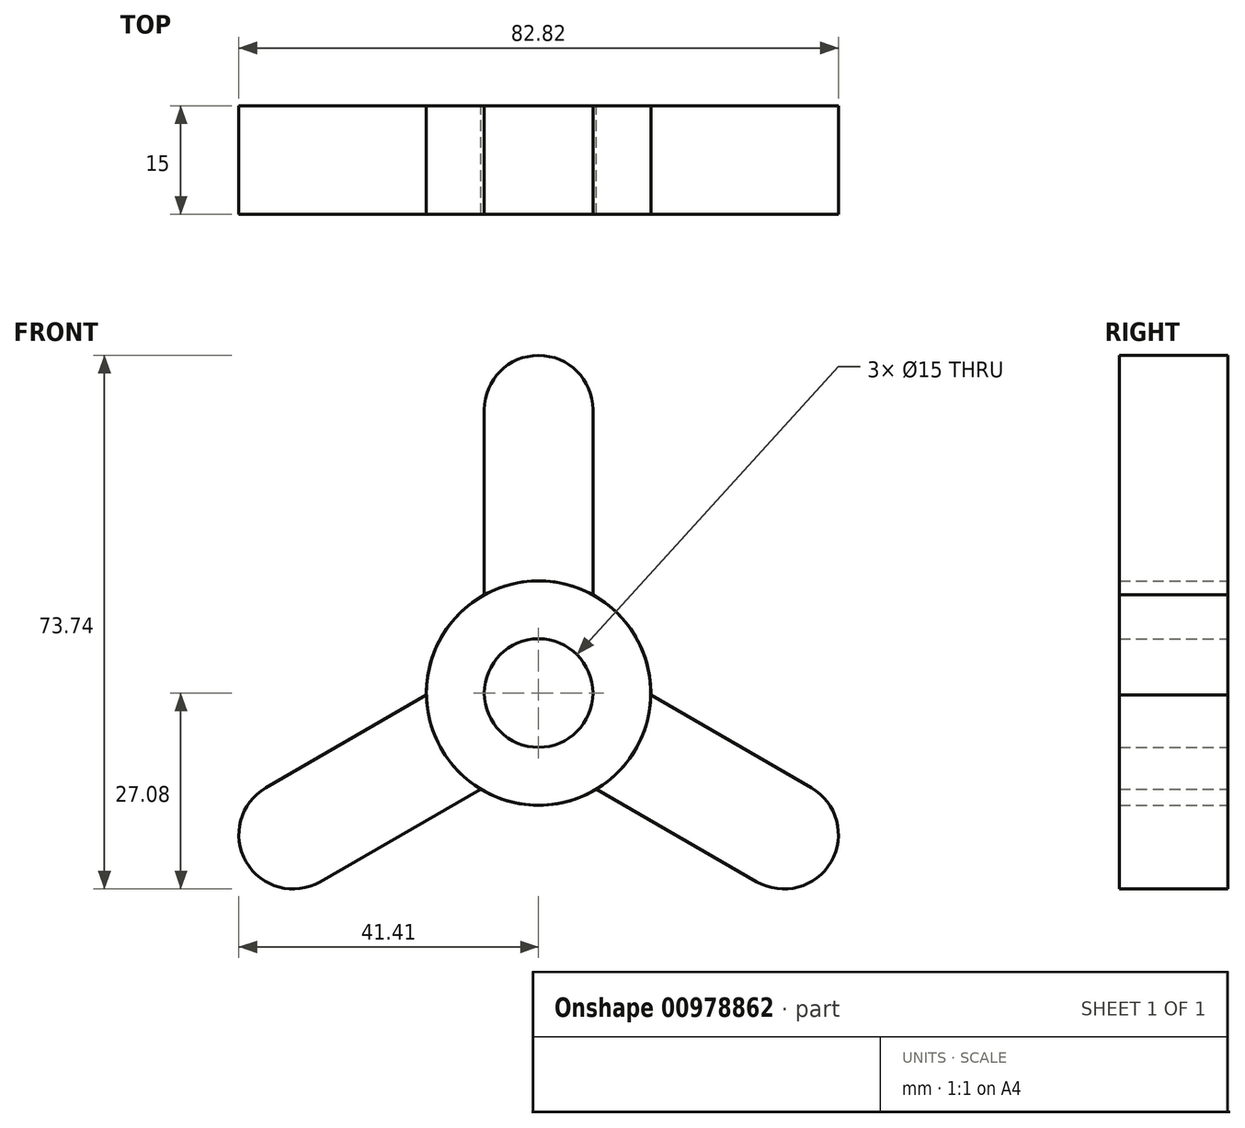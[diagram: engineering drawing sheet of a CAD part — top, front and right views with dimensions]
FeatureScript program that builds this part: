
annotation { "Feature Type Name" : "Feature", "Feature Type Description" : "" }
export const myFeature = defineFeature(function(context is Context, id is Id, definition is map)
    precondition{}
    {
        {
            var Q0;
            Q0=qCreatedBy(makeId("Front.planeOp"),FACE);
            var sketch = newSketch(context, id + "F0", { "sketchPlane" : qUnion([Q0])});
            skCircle(sketch, "E0", {"center": v(0, 0) * mm, "radius": 7.5 * mm});
            skCircle(sketch, "E1.0", {"center": v(0, 0) * mm, "radius": 15.5 * mm});
            skSolve(sketch);
        }
        {
            var Q0;
            Q0 = qSketchRegion(id + "F0", true);
            extrude(context, id + "F1", {"entities" : qUnion([Q0]), "depth" : 15 * mm, "offsetDistance" : 25 * mm});
        }
        {
            var Q0;
            Q0=qCreatedBy(makeId("Front.planeOp"),FACE);
            var sketch = newSketch(context, id + "F2", { "sketchPlane" : qUnion([Q0])});
            skArc(sketch, "E2.0.startCap", {"start": v(-7.5, 39.16) * mm, "mid": v(0, 46.66) * mm, "end": v(7.5, 39.16) * mm});
            skLineSegment(sketch, "E2.0.left", {"start": v(7.5, 39.16) * mm, "end": v(7.5, 13.56) * mm});
            skLineSegment(sketch, "E2.0.right", {"start": v(-7.5, 39.16) * mm, "end": v(-7.5, 13.56) * mm});
            skArc(sketch, "E3.0", {"start": v(7.5, 13.56) * mm, "mid": v(0, 15.5) * mm, "end": v(-7.5, 13.56) * mm});
            skSolve(sketch);
        }
        {
            var Q0;
            Q0 = qSketchRegion(id + "F2", true);
            var Q1;
            Q1=makeQuery(id+"F1.opExtrude","CAP_FACE",FACE,{"disambiguationData":[OSD([sQuery(id+"F0.wireOp",EDGE,"E0"),sQuery(id+"F0.wireOp",EDGE,"E1.0")])],"isStart":false});
            extrude(context, id + "F3", {"entities" : qUnion([Q0]), "operationType" : NewBodyOperationType.ADD, "endBound" : BoundingType.UP_TO_SURFACE, "depth" : 25 * mm, "endBoundEntityFace" : qUnion([Q1]), "offsetDistance" : 25 * mm});
        }
        {
            var Q0;
            Q0=makeQuery(id+"F1.opExtrude","SWEPT_BODY",BODY,{"disambiguationData":[OSD([sQuery(id+"F0.wireOp",EDGE,"E0"),sQuery(id+"F0.wireOp",EDGE,"E1.0")])]});
            var Q1;
            Q1=makeQuery(id+"F1.opExtrude","CAP_EDGE",EDGE,{"disambiguationData":[OSD([sQuery(id+"F0.wireOp",EDGE,"E0")])],"isStart":false});
            circularPattern(context, id + "F4", {"entities" : qUnion([Q0]), "axis" : qUnion([Q1]), "angle" : 360 * degree, "instanceCount" : 3, "equalSpace" : true});
        }
    });
